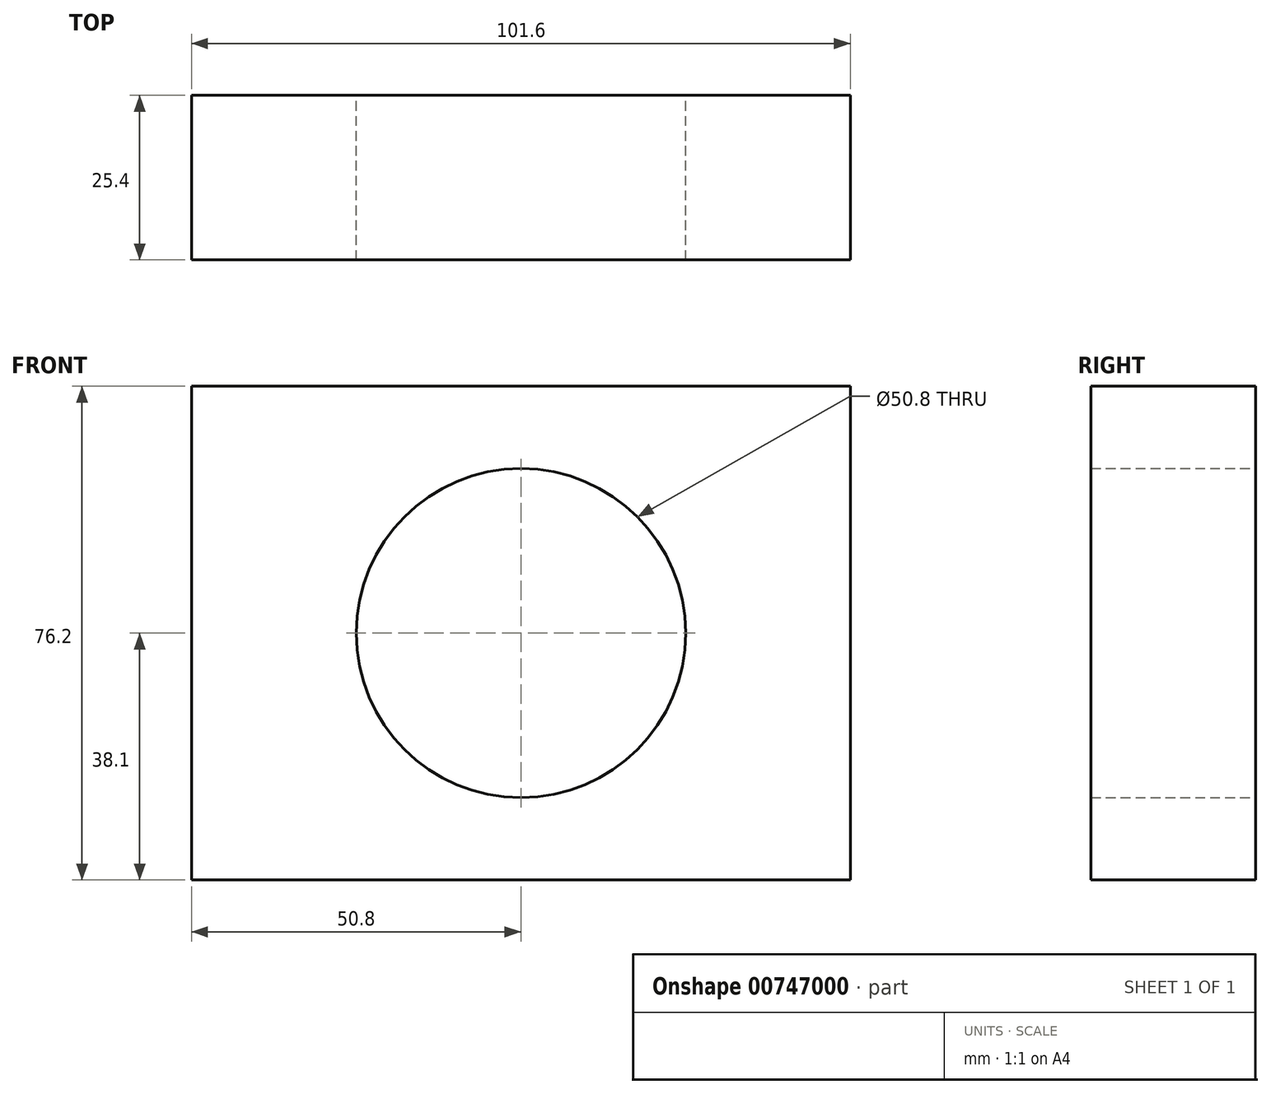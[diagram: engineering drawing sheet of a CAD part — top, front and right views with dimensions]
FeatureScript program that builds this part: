
annotation { "Feature Type Name" : "Feature", "Feature Type Description" : "" }
export const myFeature = defineFeature(function(context is Context, id is Id, definition is map)
    precondition{}
    {
        {
            var Q0;
            Q0=qCreatedBy(makeId("Front.planeOp"),FACE);
            var sketch = newSketch(context, id + "F0", { "sketchPlane" : qUnion([Q0])});
            skLineSegment(sketch, "E0.bottom", {"start": v(0, 0) * mm, "end": v(101.6, 0) * mm});
            skLineSegment(sketch, "E0.top", {"start": v(0, 76.2) * mm, "end": v(101.6, 76.2) * mm});
            skLineSegment(sketch, "E0.left", {"start": v(0, 0) * mm, "end": v(0, 76.2) * mm});
            skLineSegment(sketch, "E0.right", {"start": v(101.6, 0) * mm, "end": v(101.6, 76.2) * mm});
            skSolve(sketch);
        }
        {
            var Q0;
            Q0 = qSketchRegion(id + "F0", true);
            extrude(context, id + "F1", {"entities" : qUnion([Q0]), "depth" : 25.4 * mm, "offsetDistance" : 25.4 * mm});
        }
        {
            var Q0;
            Q0=makeQuery(id+"F1.opExtrude","CAP_FACE",FACE,{"disambiguationData":[OSD([sQuery(id+"F0.wireOp",EDGE,"E0.bottom"),sQuery(id+"F0.wireOp",EDGE,"E0.top"),sQuery(id+"F0.wireOp",EDGE,"E0.left"),sQuery(id+"F0.wireOp",EDGE,"E0.right")])],"isStart":true});
            var sketch = newSketch(context, id + "F2", { "sketchPlane" : qUnion([Q0])});
            skCircle(sketch, "E1", {"center": v(-50.8, 38.1) * mm, "radius": 25.4 * mm});
            skSolve(sketch);
        }
        {
            var Q0;
            Q0=makeQuery(id+"F2.imprint","IMPRINT",FACE,{"disambiguationData":[TD([[makeQuery(id+"F2.imprint","IMPRINT",EDGE,{"derivedFrom":sQuery(id+"F2.wireOp",EDGE,"E1")}),1.0]])]});
            extrude(context, id + "F3", {"entities" : qUnion([Q0]), "operationType" : NewBodyOperationType.REMOVE, "endBound" : BoundingType.THROUGH_ALL, "oppositeDirection" : true, "depth" : 25.4 * mm, "offsetDistance" : 25.4 * mm});
        }
    });
